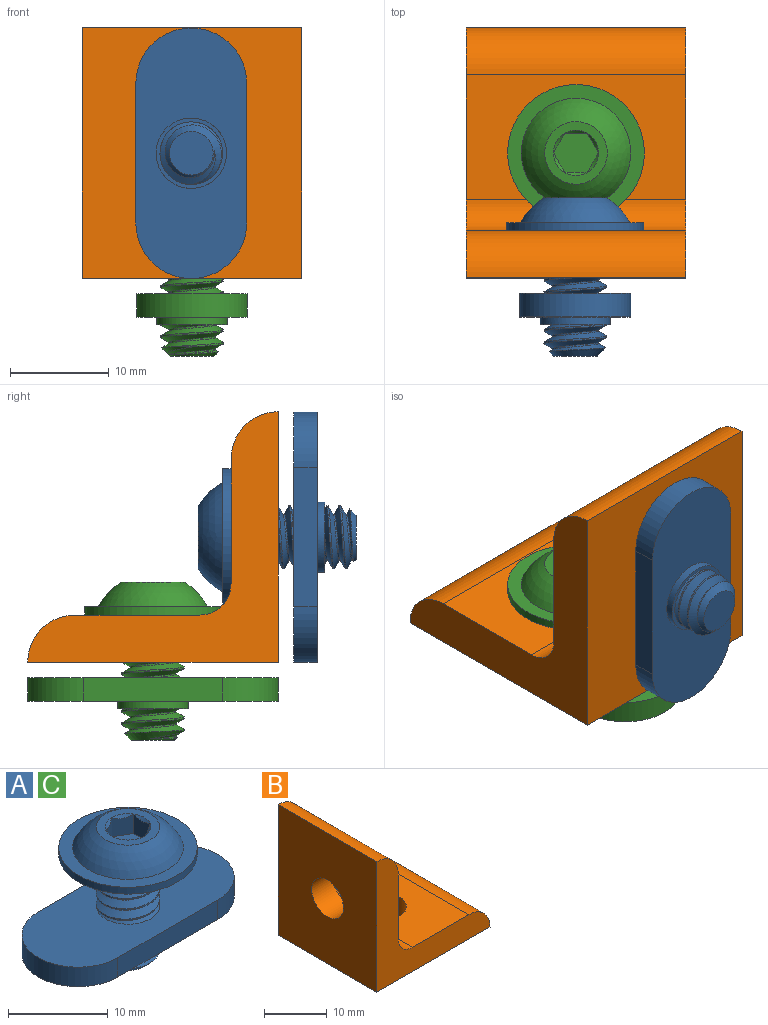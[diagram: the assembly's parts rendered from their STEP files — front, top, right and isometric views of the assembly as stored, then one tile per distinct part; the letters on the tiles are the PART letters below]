
ASSEMBLY  parts=3 mates=2
PART A: 34 faces, bbox 26.3x14.7x17 mm
  f0: cylinder r=3.17mm len=6.35mm, axis (0,0,1), area 15.5mm2, adj f2,f4,f7,f31
  f1: cylinder r=3.17mm len=6.35mm, axis (0,0,1), area 5.6mm2, adj f2,f4,f5,f32
  f2: bspline ~13.37x6.49mm, area 142.3mm2, adj f0,f1,f3,f5,f7,f25
  f3: cylinder r=2.35mm len=12.56mm, axis (0,0,1), area 13.7mm2, adj f2,f4,f5,f7
  f4: bspline ~13.22x6.49mm, area 158.7mm2, adj f0,f1,f3,f5,f7,f25
  f5: cone r=2.21mm half-angle=45deg, axis (0,0,1), area 12.5mm2, adj f1,f2,f3,f4,f6
  f6: plane 4.43x4.43mm, normal (0,0,-1), area 15.4mm2, adj f5
  f7: plane 14.36x14.36mm, normal (0,0,-1), area 126.8mm2, adj f0,f2,f3,f4,f11
  f8: plane 6.35x6.35mm, normal (0,0,1), area 15.2mm2, adj f9,f12,f13,f14,f15,f16,f17
  f9: sphere r=6.24mm, area 98.7mm2, adj f8,f10
  f10: plane 13.87x13.87mm, normal (0,0,1), area 54.3mm2, adj f9,f11
  f11: cylinder r=6.93mm len=13.87mm, axis (0,0,-1), area 36.5mm2, adj f7,f10
  f12: cone r=2.29mm half-angle=45deg, axis (0,0,1), area 0mm2, adj f8,f19
  f13: cone r=2.29mm half-angle=45deg, axis (0,0,1), area 0mm2, adj f8,f20
  f14: cone r=2.29mm half-angle=45deg, axis (0,0,1), area 0mm2, adj f8,f21
  f15: cone r=2.29mm half-angle=45deg, axis (0,0,1), area 0mm2, adj f8,f22
  f16: cone r=2.29mm half-angle=45deg, axis (0,0,1), area 0mm2, adj f8,f23
  f17: cone r=2.29mm half-angle=45deg, axis (0,0,1), area 0mm2, adj f8,f24
  f18: plane 4.58x3.97mm, normal (0,0,1), area 13.6mm2, adj f19,f20,f21,f22,f23,f24
  f19: plane 3.25x2.85mm, normal (0.5,-0.87,0), area 5mm2, adj f12,f18,f20,f24
  f20: plane 3.25x3.16mm, normal (1,0,0), area 5mm2, adj f13,f18,f19,f21
  f21: plane 3.25x2.85mm, normal (0.5,0.87,0), area 5mm2, adj f14,f18,f20,f22
  f22: plane 3.25x2.85mm, normal (-0.5,0.87,0), area 5mm2, adj f15,f18,f21,f23
  f23: plane 3.25x3.16mm, normal (-1,0,0), area 5mm2, adj f16,f18,f22,f24
  f24: plane 3.25x2.85mm, normal (-0.5,-0.87,0), area 5mm2, adj f17,f18,f19,f23
  f25: cylinder r=3.17mm len=6.35mm, axis (0,0,1), area 55mm2, adj f2,f4,f31,f32
  f26: plane 25.4x11.25mm, normal (0,0,-1), area 218.6mm2, adj f27,f28,f29,f30,f33
  f27: cylinder r=5.63mm len=11.25mm, axis (0,0,1), area 42.2mm2, adj f26,f28,f30,f31
  f28: plane 14.15x2.39mm, normal (0,1,0), area 33.8mm2, adj f26,f27,f29,f31
  f29: cylinder r=5.63mm len=11.25mm, axis (0,0,1), area 42.2mm2, adj f26,f28,f30,f31
  f30: plane 14.15x2.39mm, normal (0,-1,0), area 33.8mm2, adj f26,f27,f29,f31
  f31: plane 25.4x11.25mm, normal (0,0,1), area 227mm2, adj f0,f25,f27,f28,f29,f30
  f32: plane 7.14x7.14mm, normal (0,0,-1), area 8.3mm2, adj f1,f25,f33
  f33: cylinder r=3.57mm len=7.14mm, axis (0,0,1), area 17.1mm2, adj f26,f32
PART B: 11 faces, bbox 25.4x22.2x25.4 mm
  f0: plane 22.23x12.67mm, normal (1,0,0), area 241.7mm2, adj f5,f6,f7,f8,f10
  f1: plane 25.4x22.23mm, normal (-1,0,0), area 524.5mm2, adj f2,f6,f7,f8,f10
  f2: plane 25.4x22.23mm, normal (0,0,-1), area 524.5mm2, adj f1,f4,f7,f8,f9
  f3: plane 22.23x12.67mm, normal (0,0,1), area 241.7mm2, adj f4,f5,f7,f8,f9
  f4: cylinder r=4.78mm len=22.23mm, axis (0,1,0), area 166.7mm2, adj f2,f3,f7,f8
  f5: cylinder r=3.17mm len=22.23mm, axis (0,1,0), area 110.8mm2, adj f0,f3,f7,f8
  f6: cylinder r=4.78mm len=22.23mm, axis (0,1,0), area 166.7mm2, adj f0,f1,f7,f8
  f7: plane 25.4x25.4mm, normal (0,-1,0), area 212.2mm2, adj f0,f1,f2,f3,f4,f5,f6
  f8: plane 25.4x25.4mm, normal (0,1,0), area 212.2mm2, adj f0,f1,f2,f3,f4,f5,f6
  f9: cylinder r=3.57mm len=7.14mm, axis (0,0,-1), area 107.1mm2, adj f2,f3
  f10: cylinder r=3.57mm len=7.14mm, axis (-1,0,0), area 107.1mm2, adj f0,f1
PART C: same geometry as A
PLACE A rot(axis=(-0.58,0.58,0.58),120deg) t=(-11.18,4.78,12.67)mm
PLACE B rot(axis=(0,0,1),90deg) t=(-11.11,0,0)mm fixed
PLACE C rot(axis=(0,0,-1),90deg) t=(-11.11,12.7,4.78)mm
MATE fastened C.f0 <-> B.f9  axis (0,0,-1) through (-11.11,12.7,4.78)mm
MATE fastened A.f7 <-> B.f10  axis (0,-1,0) through (-11.11,4.78,12.7)mm
